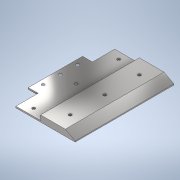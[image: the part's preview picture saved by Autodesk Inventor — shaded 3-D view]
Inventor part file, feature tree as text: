
AUTODESK INVENTOR PART (.ipt)
format: ipt  version: 2021 (Build 250183000, 183)  size: 178,176 bytes
history: native  units: mm
features: sketch x5, other x3, extrude x3, hole x2, chamfer x1
ambient origin geometry x8: Origin, YZ Plane, XZ Plane, XY Plane, X Axis, Y Axis, Z Axis, Center Point
bodies: Body1 (feature_tree)
feature tree (14):
  other  "Sólido1"
  extrude  "Extrusão1"  Depth=100.0mm
  extrude  "Extrusão2"  Depth=25.0mm
  extrude  "Extrusão3"  Depth=1.5mm
  hole  "Furo3"  [1 undecoded]
  chamfer  "Chanfro1"  [1 undecoded]
  hole  "Furo4"  [1 undecoded]
  sketch  "Esboço1"  dims[d0=70.0mm d1=100.0mm]
  sketch  "Esboço2"  dims[d2=6.35mm d3=0.0mm d7=25.0mm]
  other  "Contorno projetado1"
  sketch  "Esboço3"  dims[d8=4.886922mm d9=1.5mm]
  other  "Contorno projetado2"
  sketch  "Esboço10"  dims[d10=0.0mm d11=0.0mm d12=10.0mm]
  sketch  "Esboço11"  dims[d13=55.0mm d14=0.0mm d15=0.0mm d16=35.0mm d61=10.0mm d62=10.0mm d63=50.0mm d64=5.0mm d65=3.0mm d66=6.0mm d67=4.0mm d68=2.0mm d69=90.0deg d70=8.0mm d71=20.594885mm d72=1.5mm d73=2.0mm d74=45.0deg d75=10.0mm d76=35.0mm d77=35.0mm d78=29.0mm d79=43.0mm d80=43.0mm d81=3.0mm d82=6.0mm d83=4.0mm d84=2.0mm d85=90.0deg d86=8.0mm d87=20.594885mm]
note: 3 required parameter values undecoded (feature->parameter linkage not recoverable at this tier; creation-order binding heuristic only, values carry confidence <= 0.55)
